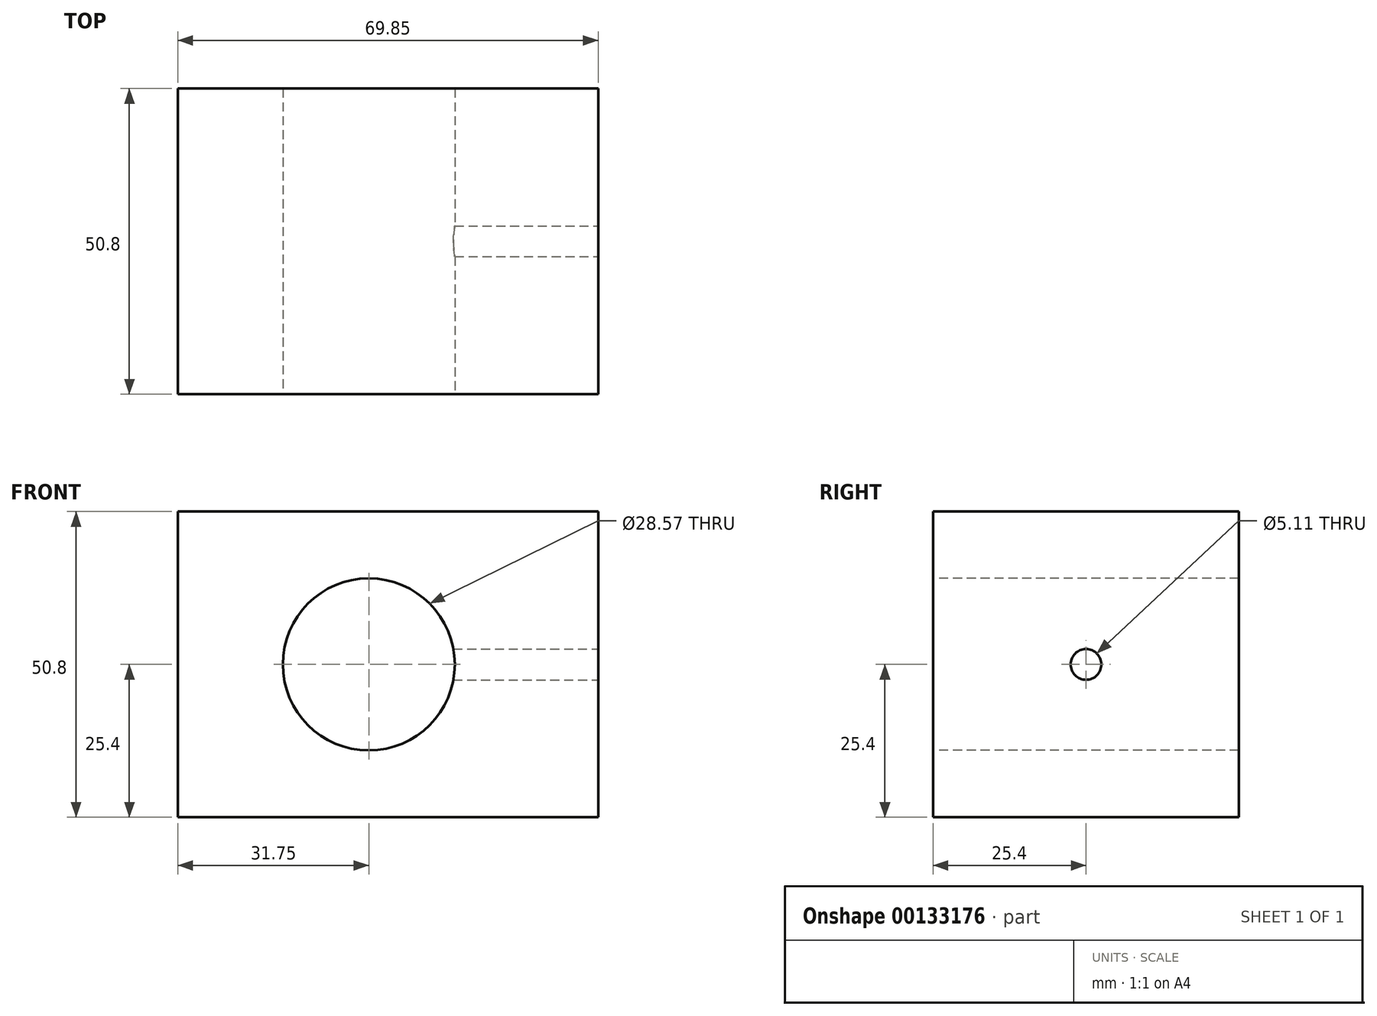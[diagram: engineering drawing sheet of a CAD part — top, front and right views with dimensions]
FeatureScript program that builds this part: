
annotation { "Feature Type Name" : "Feature", "Feature Type Description" : "" }
export const myFeature = defineFeature(function(context is Context, id is Id, definition is map)
    precondition{}
    {
        {
            var Q0;
            Q0=qCreatedBy(makeId("Front.planeOp"),FACE);
            var sketch = newSketch(context, id + "F0", { "sketchPlane" : qUnion([Q0])});
            skLineSegment(sketch, "E0.bottom", {"start": v(0, 0) * mm, "end": v(69.85, 0) * mm});
            skLineSegment(sketch, "E0.top", {"start": v(0, 50.8) * mm, "end": v(69.85, 50.8) * mm});
            skLineSegment(sketch, "E0.left", {"start": v(0, 0) * mm, "end": v(0, 50.8) * mm});
            skLineSegment(sketch, "E0.right", {"start": v(69.85, 0) * mm, "end": v(69.85, 50.8) * mm});
            skSolve(sketch);
        }
        {
            var Q0;
            Q0 = qSketchRegion(id + "F0", true);
            extrude(context, id + "F1", {"entities" : qUnion([Q0]), "depth" : 50.8 * mm});
        }
        {
            var Q0;
            Q0=makeQuery(id+"F1.opExtrude","CAP_FACE",FACE,{"disambiguationData":[OSD([sQuery(id+"F0.wireOp",EDGE,"E0.bottom"),sQuery(id+"F0.wireOp",EDGE,"E0.top"),sQuery(id+"F0.wireOp",EDGE,"E0.left"),sQuery(id+"F0.wireOp",EDGE,"E0.right")])],"isStart":false});
            var sketch = newSketch(context, id + "F2", { "sketchPlane" : qUnion([Q0])});
            skCircle(sketch, "E1", {"center": v(31.75, 25.4) * mm, "radius": 14.29 * mm});
            skSolve(sketch);
        }
        {
            var Q0;
            Q0 = qSketchRegion(id + "F2", true);
            extrude(context, id + "F3", {"entities" : qUnion([Q0]), "operationType" : NewBodyOperationType.REMOVE, "endBound" : BoundingType.THROUGH_ALL, "oppositeDirection" : true, "depth" : 25.4 * mm});
        }
        {
            var Q0;
            Q0=makeQuery(id+"F1.opExtrude","SWEPT_FACE",FACE,{"disambiguationData":[OSD([sQuery(id+"F0.wireOp",EDGE,"E0.right")])]});
            var sketch = newSketch(context, id + "F4", { "sketchPlane" : qUnion([Q0])});
            skLineSegment(sketch, "E2", {"start": v(-25.4, 37.36) * mm, "end": v(-25.4, 11.47) * mm});
            skLineSegment(sketch, "E3", {"start": v(-45.07, 25.4) * mm, "end": v(-11.78, 25.4) * mm});
            skPoint(sketch, "E4", {"position": v(-25.4, 25.4) * mm});
            skSolve(sketch);
        }
        {
            var Q0;
            Q0=sQuery(id+"F4.wireOp",VERTEX,"E4");
            var Q1;
            Q1=makeQuery(id+"F1.opExtrude","SWEPT_BODY",BODY,{"disambiguationData":[OSD([sQuery(id+"F0.wireOp",EDGE,"E0.bottom"),sQuery(id+"F0.wireOp",EDGE,"E0.top"),sQuery(id+"F0.wireOp",EDGE,"E0.left"),sQuery(id+"F0.wireOp",EDGE,"E0.right")])]});
            hole(context, id + "F5", {"style" : HoleStyle.SIMPLE, "endStyle" : HoleEndStyle.BLIND, "standardTappedOrClearance" : lookupTablePath({ "standard" : "ANSI", "engagement" : "75%", "pitch" : "20 tpi", "size" : "1/4", "type" : "Tapped" }), "standardBlindInLast" : lookupTablePath({ "standard" : "ANSI", "engagement" : "75%", "pitch" : "20 tpi", "size" : "1/4", "type" : "Tapped" }), "holeDiameter" : 5.1 * mm, "holeDepth" : 25.4 * mm, "locations" : qUnion([Q0]), "scope" : qUnion([Q1]), "majorDiameter" : 6.35 * mm});
        }
    });
